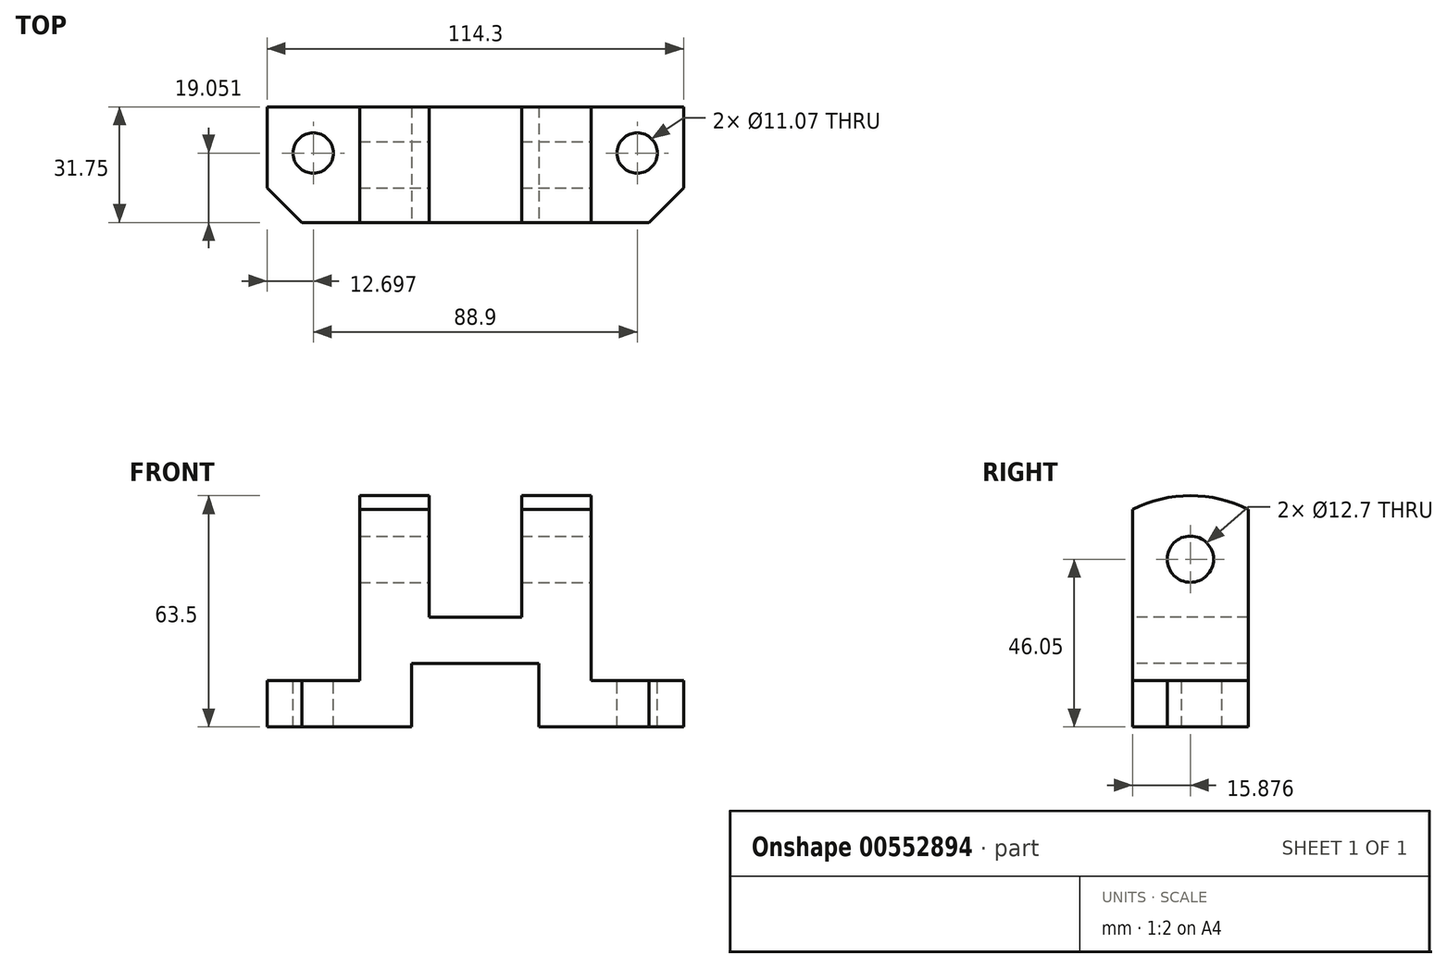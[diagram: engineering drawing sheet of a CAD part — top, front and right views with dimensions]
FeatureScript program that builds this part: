
annotation { "Feature Type Name" : "Feature", "Feature Type Description" : "" }
export const myFeature = defineFeature(function(context is Context, id is Id, definition is map)
    precondition{}
    {
        {
            var Q0;
            Q0=qCreatedBy(makeId("Top.planeOp"),FACE);
            var sketch = newSketch(context, id + "F0", { "sketchPlane" : qUnion([Q0])});
            skLineSegment(sketch, "E0.bottom", {"start": v(-12.67, 10.42) * mm, "end": v(101.63, 10.42) * mm});
            skLineSegment(sketch, "E0.top", {"start": v(-12.67, -21.33) * mm, "end": v(101.63, -21.33) * mm});
            skLineSegment(sketch, "E0.left", {"start": v(-12.67, 10.42) * mm, "end": v(-12.67, -21.33) * mm});
            skLineSegment(sketch, "E0.right", {"start": v(101.63, 10.42) * mm, "end": v(101.63, -21.33) * mm});
            skSolve(sketch);
        }
        {
            var Q0;
            Q0=makeQuery(id+"F0.imprint","IMPRINT",FACE,{"disambiguationData":[TD([[makeQuery(id+"F0.imprint","IMPRINT",EDGE,{"derivedFrom":sQuery(id+"F0.wireOp",EDGE,"E0.bottom")}),-1.0]])]});
            extrude(context, id + "F1", {"entities" : qUnion([Q0]), "depth" : 63.5 * mm, "offsetDistance" : 25.4 * mm});
        }
        {
            var Q0;
            Q0=makeQuery(id+"F1.opExtrude","SWEPT_FACE",FACE,{"disambiguationData":[OSD([sQuery(id+"F0.wireOp",EDGE,"E0.top")])]});
            var sketch = newSketch(context, id + "F2", { "sketchPlane" : qUnion([Q0])});
            skLineSegment(sketch, "E1.bottom", {"start": v(-12.67, 63.5) * mm, "end": v(12.73, 63.5) * mm});
            skLineSegment(sketch, "E1.top", {"start": v(-12.67, 12.7) * mm, "end": v(12.73, 12.7) * mm});
            skLineSegment(sketch, "E1.left", {"start": v(-12.67, 63.5) * mm, "end": v(-12.67, 12.7) * mm});
            skLineSegment(sketch, "E1.right", {"start": v(12.73, 63.5) * mm, "end": v(12.73, 12.7) * mm});
            skLineSegment(sketch, "E2.bottom", {"start": v(101.63, 63.5) * mm, "end": v(76.23, 63.5) * mm});
            skLineSegment(sketch, "E2.top", {"start": v(101.63, 12.7) * mm, "end": v(76.23, 12.7) * mm});
            skLineSegment(sketch, "E2.left", {"start": v(101.63, 63.5) * mm, "end": v(101.63, 12.7) * mm});
            skLineSegment(sketch, "E2.right", {"start": v(76.23, 63.5) * mm, "end": v(76.23, 12.7) * mm});
            skLineSegment(sketch, "E3.bottom", {"start": v(27, 0) * mm, "end": v(61.93, 0) * mm});
            skLineSegment(sketch, "E3.top", {"start": v(27, 17.48) * mm, "end": v(61.93, 17.48) * mm});
            skLineSegment(sketch, "E3.left", {"start": v(27, 0) * mm, "end": v(27, 17.48) * mm});
            skLineSegment(sketch, "E3.right", {"start": v(61.93, 0) * mm, "end": v(61.93, 17.48) * mm});
            skLineSegment(sketch, "E4.bottom", {"start": v(31.78, 63.5) * mm, "end": v(57.18, 63.5) * mm});
            skLineSegment(sketch, "E4.top", {"start": v(31.78, 30.18) * mm, "end": v(57.18, 30.18) * mm});
            skLineSegment(sketch, "E4.left", {"start": v(31.78, 63.5) * mm, "end": v(31.78, 30.18) * mm});
            skLineSegment(sketch, "E4.right", {"start": v(57.18, 63.5) * mm, "end": v(57.18, 30.18) * mm});
            skSolve(sketch);
        }
        {
            var Q0;
            Q0=makeQuery(id+"F2.imprint","IMPRINT",FACE,{"disambiguationData":[TD([[makeQuery(id+"F2.imprint","IMPRINT",EDGE,{"derivedFrom":sQuery(id+"F2.wireOp",EDGE,"E1.bottom")}),-1.0]])]});
            var Q1;
            Q1=makeQuery(id+"F2.imprint","IMPRINT",FACE,{"disambiguationData":[TD([[makeQuery(id+"F2.imprint","IMPRINT",EDGE,{"derivedFrom":sQuery(id+"F2.wireOp",EDGE,"E4.bottom")}),-1.0]])]});
            var Q2;
            Q2=makeQuery(id+"F2.imprint","IMPRINT",FACE,{"disambiguationData":[TD([[makeQuery(id+"F2.imprint","IMPRINT",EDGE,{"derivedFrom":sQuery(id+"F2.wireOp",EDGE,"E2.bottom")}),-1.0]])]});
            var Q3;
            Q3=makeQuery(id+"F2.imprint","IMPRINT",FACE,{"disambiguationData":[TD([[makeQuery(id+"F2.imprint","IMPRINT",EDGE,{"derivedFrom":sQuery(id+"F2.wireOp",EDGE,"E3.bottom")}),1.0]])]});
            extrude(context, id + "F3", {"entities" : qUnion([Q0, Q1, Q2, Q3]), "operationType" : NewBodyOperationType.REMOVE, "endBound" : BoundingType.THROUGH_ALL, "oppositeDirection" : true, "depth" : 25.4 * mm, "offsetDistance" : 25.4 * mm});
        }
        {
            var Q0;
            Q0=makeQuery(id+"F3.boolean.opBoolean","COPY",FACE,{"derivedFrom":makeQuery(id+"F3.opExtrude","SWEPT_FACE",FACE,{"disambiguationData":[OSD([sQuery(id+"F2.wireOp",EDGE,"E2.right")])]})});
            var sketch = newSketch(context, id + "F4", { "sketchPlane" : qUnion([Q0])});
            skCircle(sketch, "E5", {"center": v(-5.45, 46.05) * mm, "radius": 6.35 * mm});
            skPoint(sketch, "E5.centerSnap0", {"position": v(-5.45, 63.5) * mm});
            skSolve(sketch);
        }
        {
            var Q0;
            Q0=makeQuery(id+"F4.imprint","IMPRINT",FACE,{"disambiguationData":[TD([[makeQuery(id+"F4.imprint","IMPRINT",EDGE,{"derivedFrom":sQuery(id+"F4.wireOp",EDGE,"E5")}),1.0]])]});
            extrude(context, id + "F5", {"entities" : qUnion([Q0]), "operationType" : NewBodyOperationType.REMOVE, "endBound" : BoundingType.THROUGH_ALL, "oppositeDirection" : true, "depth" : 25.4 * mm, "offsetDistance" : 25.4 * mm});
        }
        {
            var Q0;
            Q0=makeQuery(id+"F3.boolean.opBoolean","COPY",FACE,{"derivedFrom":makeQuery(id+"F3.opExtrude","SWEPT_FACE",FACE,{"disambiguationData":[OSD([sQuery(id+"F2.wireOp",EDGE,"E1.top")])]})});
            var sketch = newSketch(context, id + "F6", { "sketchPlane" : qUnion([Q0])});
            skCircle(sketch, "E6", {"center": v(0.03, -2.28) * mm, "radius": 5.54 * mm});
            skCircle(sketch, "E7", {"center": v(88.93, -2.28) * mm, "radius": 5.54 * mm});
            skSolve(sketch);
        }
        {
            var Q0;
            Q0=makeQuery(id+"F6.imprint","IMPRINT",FACE,{"disambiguationData":[TD([[makeQuery(id+"F6.imprint","IMPRINT",EDGE,{"derivedFrom":sQuery(id+"F6.wireOp",EDGE,"E6")}),1.0]])]});
            var Q1;
            Q1=makeQuery(id+"F6.imprint","IMPRINT",FACE,{"disambiguationData":[TD([[makeQuery(id+"F6.imprint","IMPRINT",EDGE,{"derivedFrom":sQuery(id+"F6.wireOp",EDGE,"E7")}),1.0]])]});
            extrude(context, id + "F7", {"entities" : qUnion([Q0, Q1]), "operationType" : NewBodyOperationType.REMOVE, "endBound" : BoundingType.THROUGH_ALL, "oppositeDirection" : true, "depth" : 25.4 * mm, "offsetDistance" : 25.4 * mm});
        }
        {
            var Q0;
            Q0=makeQuery(id+"F3.boolean.opBoolean","COPY",FACE,{"derivedFrom":makeQuery(id+"F3.opExtrude","SWEPT_FACE",FACE,{"disambiguationData":[OSD([sQuery(id+"F2.wireOp",EDGE,"E2.right")])]})});
            var sketch = newSketch(context, id + "F8", { "sketchPlane" : qUnion([Q0])});
            skCircle(sketch, "E8", {"center": v(-5.45, 28.57) * mm, "radius": 34.93 * mm});
            skPoint(sketch, "E8.centerSnap0", {"position": v(-5.45, 12.7) * mm});
            skSolve(sketch);
        }
        {
            var Q0;
            {var subQ0=sQuery(id+"F8.wireOp",EDGE,"E8");var subQ1=sQuery(id+"F2.wireOp",EDGE,"E2.right");var subQ4=makeQuery(id+"F3.boolean.opBoolean","COPY",EDGE,{"derivedFrom":makeQuery(id+"F3.opExtrude","CAP_EDGE",EDGE,{"disambiguationData":[OSD([subQ1])],"isStart":true})});var subQ5=makeQuery(id+"F8.imprint","INTERSECT",VERTEX,{"derivedFrom":[subQ4,subQ0]});Q0=makeQuery(id+"F8.imprint","IMPRINT",FACE,{"disambiguationData":[TD([[makeQuery(id+"F8.imprint","IMPRINT",EDGE,{"disambiguationData":[TD([[subQ5,1.0]])],"derivedFrom":subQ0}),-1.0]])]});}
            var Q1;
            {var subQ0=sQuery(id+"F8.wireOp",EDGE,"E8");var subQ1=sQuery(id+"F2.wireOp",EDGE,"E2.right");var subQ4=makeQuery(id+"F3.boolean.opBoolean","INTERSECT",EDGE,{"derivedFrom":[makeQuery(id+"F1.opExtrude","SWEPT_FACE",FACE,{"disambiguationData":[OSD([sQuery(id+"F0.wireOp",EDGE,"E0.bottom")])]}),makeQuery(id+"F3.opExtrude","SWEPT_FACE",FACE,{"disambiguationData":[OSD([subQ1])]})]});var subQ5=makeQuery(id+"F8.imprint","INTERSECT",VERTEX,{"derivedFrom":[subQ4,subQ0]});Q1=makeQuery(id+"F8.imprint","IMPRINT",FACE,{"disambiguationData":[TD([[makeQuery(id+"F8.imprint","IMPRINT",EDGE,{"disambiguationData":[TD([[subQ5,-1.0]])],"derivedFrom":subQ0}),-1.0]])]});}
            extrude(context, id + "F9", {"entities" : qUnion([Q0, Q1]), "operationType" : NewBodyOperationType.REMOVE, "endBound" : BoundingType.THROUGH_ALL, "oppositeDirection" : true, "depth" : 25.4 * mm, "offsetDistance" : 25.4 * mm});
        }
        {
            var Q0;
            Q0=makeQuery(id+"F1.opExtrude","SWEPT_EDGE",EDGE,{"disambiguationData":[OSD([sQuery(id+"F0.wireOp",EDGE,"E0.top"),sQuery(id+"F0.wireOp",EDGE,"E0.right")])]});
            var Q1;
            Q1=makeQuery(id+"F1.opExtrude","SWEPT_EDGE",EDGE,{"disambiguationData":[OSD([sQuery(id+"F0.wireOp",EDGE,"E0.top"),sQuery(id+"F0.wireOp",EDGE,"E0.left")])]});
            chamfer(context, id + "F10", {"entities" : qUnion([Q0, Q1]), "width" : 9.52 * mm, "tangentPropagation" : true});
        }
    });
